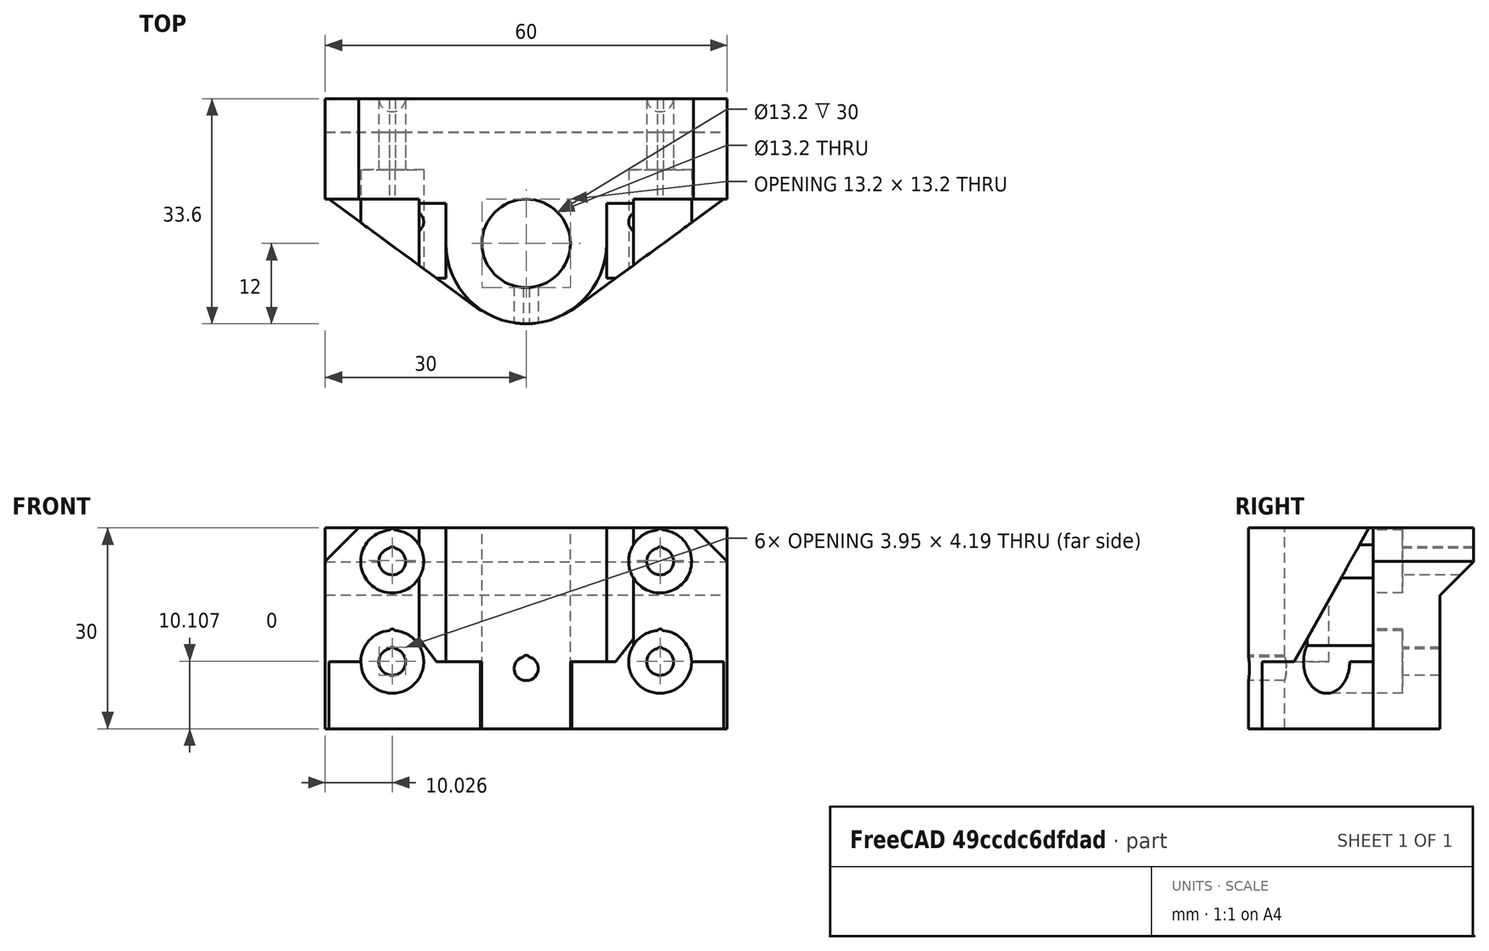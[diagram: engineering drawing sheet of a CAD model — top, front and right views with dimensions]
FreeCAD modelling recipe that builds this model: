
FCSTD DOCUMENT  (FreeCAD 0.18R14555 (Git shallow))
Label: desk-light-mounter
License: All rights reserved
LicenseURL: http://en.wikipedia.org/wiki/All_rights_reserved
objects: Part::Cylinder×20, Part::Box×8, Part::MultiFuse×8, Part::Cut×7, Part::Chamfer×4, Part::Feature×3, Part::MultiCommon×2
note: 52 computed .brp shape members not serialized (recipe doc carries the construction recipe); baked Part::Feature solids carry a one-line shape summary decoded from their .brp

FEATURE [Part::Cylinder] Cylinder
  Angle = 360
  AttacherType = Attacher::AttachEngine3D
  Height = 30
  Radius = 6.6
FEATURE [Part::Cylinder] Cylinder001
  Angle = 360
  AttacherType = Attacher::AttachEngine3D
  Height = 30
  Radius = 12
FEATURE [Part::Box] Box  label="Cube"
  AttacherType = Attacher::AttachEngine3D
  Height = 30
  Length = 60
  Placement = pos=(-30,6.6,0) rot=(0,0,1;0rad)
  Width = 10
FEATURE [Part::Box] Box001  label="Cube001"
  AttacherType = Attacher::AttachEngine3D
  Height = 30
  Length = 5.4
  Placement = pos=(6.6,0,0) rot=(0,0,1;0rad)
  Width = 7
FEATURE [Part::Box] Box002  label="Cube002"
  AttacherType = Attacher::AttachEngine3D
  Height = 30
  Length = 5.4
  Placement = pos=(-12,0,0) rot=(0,0,1;0rad)
  Width = 7
FEATURE [Part::Feature] Body001
  shape: bbox 60 x 22 x 30 mm, 5 faces (baked)
FEATURE [Part::Box] Box003  label="Cube003"
  AttacherType = Attacher::AttachEngine3D
  Height = 30
  Length = 20
  Placement = pos=(-10,-18,0) rot=(0,0,1;0rad)
  Width = 8
FEATURE [Part::Cut] Cut
  Base = -> Body001
  Tool = -> Box003
FEATURE [Part::Box] Box004  label="Cube004"
  AttacherType = Attacher::AttachEngine3D
  Height = 10
  Length = 60
  Placement = pos=(-30,-16,0) rot=(0,0,1;0rad)
  Width = 29
FEATURE [Part::Box] Box005  label="Cube005"
  AttacherType = Attacher::AttachEngine3D
  Height = 30
  Length = 4
  Placement = pos=(12,-8,0) rot=(0,0,1;0rad)
  Width = 15
FEATURE [Part::Box] Box006  label="Cube006"
  AttacherType = Attacher::AttachEngine3D
  Height = 30
  Length = 4
  Placement = pos=(-16,-8,0) rot=(0,0,1;0rad)
  Width = 15
FEATURE [Part::Chamfer] Chamfer
  Base = -> Box006
  Edges = 1 edges: [Edge10 r1=25 r2=14]
FEATURE [Part::Chamfer] Chamfer001
  Base = -> Box005
  Edges = 1 edges: [Edge10 r1=25 r2=14]
FEATURE [Part::Feature] Cut001
  shape: bbox 60 x 17 x 30 mm, 6 faces (baked)
FEATURE [Part::MultiFuse] Fusion
  Shapes = -> [Chamfer,Chamfer001]
FEATURE [Part::MultiCommon] Common
  Shapes = -> [Fusion,Cut001]
FEATURE [Part::MultiCommon] Common001
  Shapes = -> [Cut,Box004]
FEATURE [Part::MultiFuse] Fusion001
  Shapes = -> [Box,Cylinder001,Box001,Box002,Common001,Common]
FEATURE [Part::Cut] Cut002
  Base = -> Fusion001
  Tool = -> Cylinder
FEATURE [Part::Cylinder] Cylinder003
  Angle = 360
  AttacherType = Attacher::AttachEngine3D
  Height = 50
  Placement = pos=(20,20,25) rot=(1,0,0;1.5708rad)
  Radius = 0.5
FEATURE [Part::Cylinder] Cylinder004
  Angle = 360
  AttacherType = Attacher::AttachEngine3D
  Height = 50
  Placement = pos=(-20,20,10) rot=(1,0,0;1.5708rad)
  Radius = 0.5
FEATURE [Part::Cylinder] Cylinder005
  Angle = 360
  AttacherType = Attacher::AttachEngine3D
  Height = 50
  Placement = pos=(20,20,10) rot=(1,0,0;1.5708rad)
  Radius = 0.5
FEATURE [Part::Cylinder] Cylinder006
  Angle = 360
  AttacherType = Attacher::AttachEngine3D
  Height = 50
  Placement = pos=(-20,20,25) rot=(1,0,0;1.5708rad)
  Radius = 0.5
FEATURE [Part::Cylinder] Cylinder007
  Angle = 360
  AttacherType = Attacher::AttachEngine3D
  Height = 50
  Placement = pos=(20,20,25) rot=(1,0,0;1.5708rad)
  Radius = 2
FEATURE [Part::Cylinder] Cylinder008
  Angle = 360
  AttacherType = Attacher::AttachEngine3D
  Height = 50
  Placement = pos=(-20,20,10) rot=(1,0,0;1.5708rad)
  Radius = 2
FEATURE [Part::Cylinder] Cylinder009
  Angle = 360
  AttacherType = Attacher::AttachEngine3D
  Height = 50
  Placement = pos=(20,20,10) rot=(1,0,0;1.5708rad)
  Radius = 2
FEATURE [Part::Cylinder] Cylinder010
  Angle = 360
  AttacherType = Attacher::AttachEngine3D
  Height = 50
  Placement = pos=(-20,20,25) rot=(1,0,0;1.5708rad)
  Radius = 2
FEATURE [Part::MultiFuse] Fusion002
  Placement = pos=(0,10,0) rot=(0,0,1;0rad)
  Shapes = -> [Cylinder007,Cylinder008,Cylinder009,Cylinder010]
FEATURE [Part::Cylinder] Cylinder011
  Angle = 360
  AttacherType = Attacher::AttachEngine3D
  Height = 50
  Placement = pos=(-20,20,25) rot=(1,0,0;1.5708rad)
  Radius = 0.5
FEATURE [Part::Cylinder] Cylinder012
  Angle = 360
  AttacherType = Attacher::AttachEngine3D
  Height = 50
  Placement = pos=(-20,20,10) rot=(1,0,0;1.5708rad)
  Radius = 0.5
FEATURE [Part::Cylinder] Cylinder013
  Angle = 360
  AttacherType = Attacher::AttachEngine3D
  Height = 50
  Placement = pos=(20,20,25) rot=(1,0,0;1.5708rad)
  Radius = 0.5
FEATURE [Part::Cylinder] Cylinder014
  Angle = 360
  AttacherType = Attacher::AttachEngine3D
  Height = 50
  Placement = pos=(20,20,10) rot=(1,0,0;1.5708rad)
  Radius = 0.5
FEATURE [Part::MultiFuse] Fusion003
  Placement = pos=(0,10,1.7) rot=(0,0,1;0rad)
  Shapes = -> [Cylinder006,Cylinder004,Cylinder003,Cylinder005]
FEATURE [Part::Cylinder] Cylinder015
  Angle = 360
  AttacherType = Attacher::AttachEngine3D
  Height = 50
  Placement = pos=(20,20,10) rot=(1,0,0;1.5708rad)
  Radius = 4.7
FEATURE [Part::Cylinder] Cylinder016
  Angle = 360
  AttacherType = Attacher::AttachEngine3D
  Height = 50
  Placement = pos=(-20,20,25) rot=(1,0,0;1.5708rad)
  Radius = 4.7
FEATURE [Part::Cylinder] Cylinder017
  Angle = 360
  AttacherType = Attacher::AttachEngine3D
  Height = 50
  Placement = pos=(-20,20,10) rot=(1,0,0;1.5708rad)
  Radius = 4.7
FEATURE [Part::Cylinder] Cylinder018
  Angle = 360
  AttacherType = Attacher::AttachEngine3D
  Height = 50
  Placement = pos=(20,20,25) rot=(1,0,0;1.5708rad)
  Radius = 4.7
FEATURE [Part::MultiFuse] Fusion004
  Placement = pos=(0,-9,0) rot=(0,0,1;0rad)
  Shapes = -> [Cylinder015,Cylinder016,Cylinder018,Cylinder017]
FEATURE [Part::MultiFuse] Fusion005
  Placement = pos=(0,-9,4.4) rot=(0,0,1;0rad)
  Shapes = -> [Cylinder014,Cylinder011,Cylinder012,Cylinder013]
FEATURE [Part::Cylinder] Cylinder019
  Angle = 360
  AttacherType = Attacher::AttachEngine3D
  Height = 26
  Placement = pos=(0,2e-15,9) rot=(1,0,0;1.5708rad)
  Radius = 1.8
FEATURE [Part::Cylinder] Cylinder020
  Angle = 360
  AttacherType = Attacher::AttachEngine3D
  Height = 26
  Placement = pos=(0,2e-15,10.5) rot=(1,0,0;1.5708rad)
  Radius = 0.5
FEATURE [Part::MultiFuse] Fusion006
  Shapes = -> [Cylinder020,Cylinder019]
FEATURE [Part::Box] Box007  label="Cube007"
  AttacherType = Attacher::AttachEngine3D
  Height = 10
  Length = 60
  Placement = pos=(-30,16.6,20) rot=(0,0,1;0rad)
  Width = 5
FEATURE [Part::Chamfer] Chamfer002
  Base = -> Box007
  Edges = 1 edges r=4.95: [Edge11]
FEATURE [Part::MultiFuse] Fusion007
  Shapes = -> [Chamfer002,Cut002]
FEATURE [Part::Cut] Cut003
  Base = -> Fusion007
  Tool = -> Fusion002
FEATURE [Part::Cut] Cut004
  Base = -> Cut003
  Tool = -> Fusion003
FEATURE [Part::Cut] Cut005
  Base = -> Cut004
  Tool = -> Fusion004
FEATURE [Part::Cut] Cut006
  Base = -> Cut005
  Tool = -> Fusion005
FEATURE [Part::Cut] Cut007
  Base = -> Cut006
  Tool = -> Fusion006
FEATURE [Part::Feature] Cut007001  label="Cut008"
  shape: bbox 60 x 33.6 x 30 mm, 52 faces (baked)
FEATURE [Part::Chamfer] Chamfer003
  Base = -> Cut007001
  Edges = 2 edges r=5: [Edge47,Edge155]
